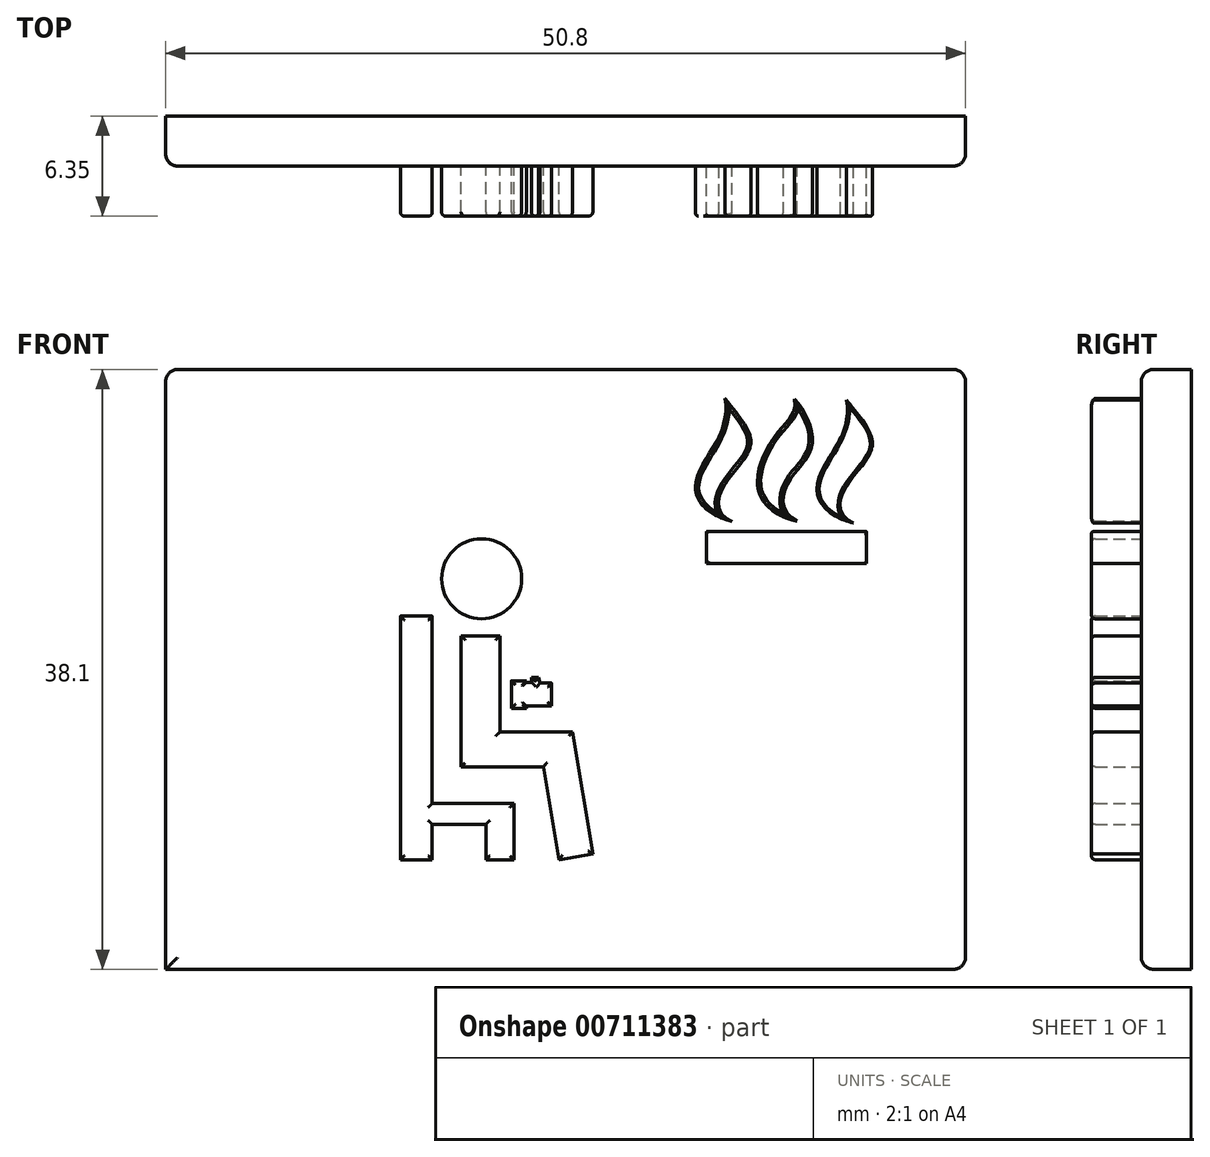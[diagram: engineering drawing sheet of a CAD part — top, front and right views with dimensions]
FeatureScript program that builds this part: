
annotation { "Feature Type Name" : "Feature", "Feature Type Description" : "" }
export const myFeature = defineFeature(function(context is Context, id is Id, definition is map)
    precondition{}
    {
        {
            var Q0;
            Q0=qCreatedBy(makeId("Front.planeOp"),FACE);
            var sketch = newSketch(context, id + "F0", { "sketchPlane" : qUnion([Q0])});
            skLineSegment(sketch, "E0.bottom", {"start": v(-18.77, 4.86) * mm, "end": v(32.03, 4.86) * mm});
            skLineSegment(sketch, "E0.top", {"start": v(-18.77, -33.24) * mm, "end": v(32.03, -33.24) * mm});
            skLineSegment(sketch, "E0.left", {"start": v(-18.77, 4.86) * mm, "end": v(-18.77, -33.24) * mm});
            skLineSegment(sketch, "E0.right", {"start": v(32.03, 4.86) * mm, "end": v(32.03, -33.24) * mm});
            skSolve(sketch);
        }
        {
            var Q0;
            Q0=makeQuery(id+"F0.imprint","IMPRINT",FACE,{"disambiguationData":[TD([[makeQuery(id+"F0.imprint","IMPRINT",EDGE,{"derivedFrom":sQuery(id+"F0.wireOp",EDGE,"E0.bottom")}),-1.0]])]});
            extrude(context, id + "F1", {"entities" : qUnion([Q0]), "depth" : 3.17 * mm, "offsetDistance" : 25.4 * mm});
        }
        {
            var Q0;
            Q0=makeQuery(id+"F1.opExtrude","CAP_FACE",FACE,{"disambiguationData":[OSD([sQuery(id+"F0.wireOp",EDGE,"E0.bottom"),sQuery(id+"F0.wireOp",EDGE,"E0.top"),sQuery(id+"F0.wireOp",EDGE,"E0.left"),sQuery(id+"F0.wireOp",EDGE,"E0.right")])],"isStart":false});
            var sketch = newSketch(context, id + "F2", { "sketchPlane" : qUnion([Q0])});
            skCircle(sketch, "E1", {"center": v(1.3, -8.43) * mm, "radius": 2.54 * mm});
            skLineSegment(sketch, "E2", {"start": v(0, -12.05) * mm, "end": v(0, -20.37) * mm});
            skLineSegment(sketch, "E3", {"start": v(0, -20.37) * mm, "end": v(5.23, -20.37) * mm});
            skLineSegment(sketch, "E4", {"start": v(5.23, -20.37) * mm, "end": v(6.22, -26.27) * mm});
            skLineSegment(sketch, "E5", {"start": v(6.22, -26.27) * mm, "end": v(8.36, -25.92) * mm});
            skLineSegment(sketch, "E6", {"start": v(8.36, -25.92) * mm, "end": v(7.07, -18.16) * mm});
            skLineSegment(sketch, "E7", {"start": v(7.07, -18.16) * mm, "end": v(2.46, -18.16) * mm});
            skLineSegment(sketch, "E8", {"start": v(2.46, -18.16) * mm, "end": v(2.46, -12.05) * mm});
            skLineSegment(sketch, "E9", {"start": v(2.46, -12.05) * mm, "end": v(0, -12.05) * mm});
            skLineSegment(sketch, "E10", {"start": v(-1.83, -12.05) * mm, "end": v(-1.83, -22.7) * mm});
            skLineSegment(sketch, "E11", {"start": v(-1.83, -22.7) * mm, "end": v(3.35, -22.7) * mm});
            skLineSegment(sketch, "E12", {"start": v(3.35, -22.7) * mm, "end": v(3.35, -26.27) * mm});
            skLineSegment(sketch, "E13", {"start": v(3.35, -26.27) * mm, "end": v(1.56, -26.27) * mm});
            skLineSegment(sketch, "E14", {"start": v(1.56, -26.27) * mm, "end": v(1.56, -24.04) * mm});
            skLineSegment(sketch, "E15", {"start": v(1.56, -24.04) * mm, "end": v(-1.83, -24.04) * mm});
            skLineSegment(sketch, "E16", {"start": v(-1.83, -24.04) * mm, "end": v(-1.83, -26.27) * mm});
            skLineSegment(sketch, "E17", {"start": v(-1.83, -26.27) * mm, "end": v(-3.86, -26.27) * mm});
            skLineSegment(sketch, "E18", {"start": v(-3.86, -26.27) * mm, "end": v(-3.86, -10.8) * mm});
            skLineSegment(sketch, "E19", {"start": v(-3.86, -10.8) * mm, "end": v(-1.83, -10.8) * mm});
            skLineSegment(sketch, "E20", {"start": v(-1.83, -10.8) * mm, "end": v(-1.83, -12.05) * mm});
            skLineSegment(sketch, "E21.bottom", {"start": v(3.2, -14.9) * mm, "end": v(4.14, -14.9) * mm});
            skLineSegment(sketch, "E21.top", {"start": v(3.2, -16.65) * mm, "end": v(4.14, -16.65) * mm});
            skLineSegment(sketch, "E21.left", {"start": v(3.2, -14.9) * mm, "end": v(3.2, -16.65) * mm});
            skLineSegment(sketch, "E21.right", {"start": v(4.14, -14.9) * mm, "end": v(4.14, -16.65) * mm});
            skLineSegment(sketch, "E22", {"start": v(4.14, -15) * mm, "end": v(4.46, -15) * mm});
            skLineSegment(sketch, "E23", {"start": v(4.46, -15) * mm, "end": v(4.46, -14.7) * mm});
            skLineSegment(sketch, "E24", {"start": v(4.46, -14.7) * mm, "end": v(4.92, -14.7) * mm});
            skLineSegment(sketch, "E25", {"start": v(4.92, -14.7) * mm, "end": v(5, -15.05) * mm});
            skLineSegment(sketch, "E26", {"start": v(5, -15.05) * mm, "end": v(5.76, -15.05) * mm});
            skLineSegment(sketch, "E27", {"start": v(5.76, -15.05) * mm, "end": v(5.76, -16.52) * mm});
            skLineSegment(sketch, "E28", {"start": v(5.76, -16.52) * mm, "end": v(4.14, -16.52) * mm});
            skSolve(sketch);
        }
        {
            var Q0;
            Q0=makeQuery(id+"F2.imprint","IMPRINT",FACE,{"disambiguationData":[TD([[makeQuery(id+"F2.imprint","IMPRINT",EDGE,{"derivedFrom":sQuery(id+"F2.wireOp",EDGE,"E2")}),1.0]])]});
            var Q1;
            Q1=makeQuery(id+"F2.imprint","IMPRINT",FACE,{"disambiguationData":[TD([[makeQuery(id+"F2.imprint","IMPRINT",EDGE,{"derivedFrom":sQuery(id+"F2.wireOp",EDGE,"E10")}),-1.0]])]});
            var Q2;
            Q2=makeQuery(id+"F2.imprint","IMPRINT",FACE,{"disambiguationData":[TD([[makeQuery(id+"F2.imprint","IMPRINT",EDGE,{"derivedFrom":sQuery(id+"F2.wireOp",EDGE,"E1")}),1.0]])]});
            extrude(context, id + "F3", {"entities" : qUnion([Q0, Q1, Q2]), "operationType" : NewBodyOperationType.ADD, "depth" : 3.17 * mm, "offsetDistance" : 25.4 * mm});
        }
        {
            var Q0;
            Q0 = qSketchRegion(id + "F2", true);
            extrude(context, id + "F4", {"entities" : qUnion([Q0]), "operationType" : NewBodyOperationType.ADD, "depth" : 3.17 * mm, "offsetDistance" : 25.4 * mm});
        }
        {
            var Q0;
            Q0=makeQuery(id+"F3.opExtrude","CAP_EDGE",EDGE,{"disambiguationData":[OSD([sQuery(id+"F2.wireOp",EDGE,"E18")])],"isStart":false});
            var Q1;
            Q1=makeQuery(id+"F3.opExtrude","CAP_EDGE",EDGE,{"disambiguationData":[OSD([sQuery(id+"F2.wireOp",EDGE,"E19")])],"isStart":false});
            var Q2;
            Q2=makeQuery(id+"F3.opExtrude","CAP_EDGE",EDGE,{"disambiguationData":[OSD([sQuery(id+"F2.wireOp",EDGE,"E10"),sQuery(id+"F2.wireOp",EDGE,"E20")])],"isStart":false});
            var Q3;
            Q3=makeQuery(id+"F3.opExtrude","CAP_EDGE",EDGE,{"disambiguationData":[OSD([sQuery(id+"F2.wireOp",EDGE,"E1")])],"isStart":false});
            var Q4;
            Q4=makeQuery(id+"F3.opExtrude","CAP_EDGE",EDGE,{"disambiguationData":[OSD([sQuery(id+"F2.wireOp",EDGE,"E2")])],"isStart":false});
            var Q5;
            Q5=makeQuery(id+"F3.opExtrude","CAP_EDGE",EDGE,{"disambiguationData":[OSD([sQuery(id+"F2.wireOp",EDGE,"E9")])],"isStart":false});
            var Q6;
            Q6=makeQuery(id+"F3.opExtrude","CAP_EDGE",EDGE,{"disambiguationData":[OSD([sQuery(id+"F2.wireOp",EDGE,"E8")])],"isStart":false});
            var Q7;
            Q7=makeQuery(id+"F3.opExtrude","CAP_EDGE",EDGE,{"disambiguationData":[OSD([sQuery(id+"F2.wireOp",EDGE,"E7")])],"isStart":false});
            var Q8;
            Q8=makeQuery(id+"F3.opExtrude","CAP_EDGE",EDGE,{"disambiguationData":[OSD([sQuery(id+"F2.wireOp",EDGE,"E6")])],"isStart":false});
            var Q9;
            Q9=makeQuery(id+"F3.opExtrude","CAP_EDGE",EDGE,{"disambiguationData":[OSD([sQuery(id+"F2.wireOp",EDGE,"E5")])],"isStart":false});
            var Q10;
            Q10=makeQuery(id+"F3.opExtrude","CAP_EDGE",EDGE,{"disambiguationData":[OSD([sQuery(id+"F2.wireOp",EDGE,"E4")])],"isStart":false});
            var Q11;
            Q11=makeQuery(id+"F3.opExtrude","CAP_EDGE",EDGE,{"disambiguationData":[OSD([sQuery(id+"F2.wireOp",EDGE,"E3")])],"isStart":false});
            var Q12;
            Q12=makeQuery(id+"F3.opExtrude","CAP_EDGE",EDGE,{"disambiguationData":[OSD([sQuery(id+"F2.wireOp",EDGE,"E17")])],"isStart":false});
            var Q13;
            Q13=makeQuery(id+"F3.opExtrude","CAP_EDGE",EDGE,{"disambiguationData":[OSD([sQuery(id+"F2.wireOp",EDGE,"E16")])],"isStart":false});
            var Q14;
            Q14=makeQuery(id+"F3.opExtrude","CAP_EDGE",EDGE,{"disambiguationData":[OSD([sQuery(id+"F2.wireOp",EDGE,"E15")])],"isStart":false});
            var Q15;
            Q15=makeQuery(id+"F3.opExtrude","CAP_EDGE",EDGE,{"disambiguationData":[OSD([sQuery(id+"F2.wireOp",EDGE,"E11")])],"isStart":false});
            var Q16;
            Q16=makeQuery(id+"F3.opExtrude","CAP_EDGE",EDGE,{"disambiguationData":[OSD([sQuery(id+"F2.wireOp",EDGE,"E14")])],"isStart":false});
            var Q17;
            Q17=makeQuery(id+"F3.opExtrude","CAP_EDGE",EDGE,{"disambiguationData":[OSD([sQuery(id+"F2.wireOp",EDGE,"E13")])],"isStart":false});
            var Q18;
            Q18=makeQuery(id+"F3.opExtrude","CAP_EDGE",EDGE,{"disambiguationData":[OSD([sQuery(id+"F2.wireOp",EDGE,"E12")])],"isStart":false});
            var Q19;
            Q19=makeQuery(id+"F4.opExtrude","CAP_EDGE",EDGE,{"disambiguationData":[OSD([sQuery(id+"F2.wireOp",EDGE,"E28")])],"isStart":false});
            var Q20;
            Q20=makeQuery(id+"F4.opExtrude","CAP_EDGE",EDGE,{"disambiguationData":[OSD([sQuery(id+"F2.wireOp",EDGE,"E21.top")])],"isStart":false});
            var Q21;
            {var subQ0=sQuery(id+"F2.wireOp",EDGE,"E21.right");Q21=makeQuery(id+"F4.opExtrude","CAP_EDGE",EDGE,{"disambiguationData":[OSD([subQ0]),TDD([makeQuery(id+"F2.imprint","IMPRINT",EDGE,{"disambiguationData":[TD([[makeQuery(id+"F2.imprint","INTERSECT",VERTEX,{"derivedFrom":[sQuery(id+"F2.wireOp",EDGE,"E21.top"),subQ0]}),1.0]])],"derivedFrom":subQ0})])],"isStart":false});}
            var Q22;
            Q22=makeQuery(id+"F4.opExtrude","CAP_EDGE",EDGE,{"disambiguationData":[OSD([sQuery(id+"F2.wireOp",EDGE,"E27")])],"isStart":false});
            var Q23;
            Q23=makeQuery(id+"F4.opExtrude","CAP_EDGE",EDGE,{"disambiguationData":[OSD([sQuery(id+"F2.wireOp",EDGE,"E26")])],"isStart":false});
            var Q24;
            Q24=makeQuery(id+"F4.opExtrude","CAP_EDGE",EDGE,{"disambiguationData":[OSD([sQuery(id+"F2.wireOp",EDGE,"E25")])],"isStart":false});
            var Q25;
            Q25=makeQuery(id+"F4.opExtrude","CAP_EDGE",EDGE,{"disambiguationData":[OSD([sQuery(id+"F2.wireOp",EDGE,"E24")])],"isStart":false});
            var Q26;
            Q26=makeQuery(id+"F4.opExtrude","CAP_EDGE",EDGE,{"disambiguationData":[OSD([sQuery(id+"F2.wireOp",EDGE,"E23")])],"isStart":false});
            var Q27;
            Q27=makeQuery(id+"F4.opExtrude","CAP_EDGE",EDGE,{"disambiguationData":[OSD([sQuery(id+"F2.wireOp",EDGE,"E22")])],"isStart":false});
            var Q28;
            {var subQ0=sQuery(id+"F2.wireOp",EDGE,"E21.right");Q28=makeQuery(id+"F4.opExtrude","CAP_EDGE",EDGE,{"disambiguationData":[OSD([subQ0]),TDD([makeQuery(id+"F2.imprint","IMPRINT",EDGE,{"disambiguationData":[TD([[makeQuery(id+"F2.imprint","INTERSECT",VERTEX,{"derivedFrom":[sQuery(id+"F2.wireOp",EDGE,"E21.bottom"),subQ0]}),-1.0]])],"derivedFrom":subQ0})])],"isStart":false});}
            var Q29;
            Q29=makeQuery(id+"F4.opExtrude","CAP_EDGE",EDGE,{"disambiguationData":[OSD([sQuery(id+"F2.wireOp",EDGE,"E21.bottom")])],"isStart":false});
            var Q30;
            Q30=makeQuery(id+"F4.opExtrude","CAP_EDGE",EDGE,{"disambiguationData":[OSD([sQuery(id+"F2.wireOp",EDGE,"E21.left")])],"isStart":false});
            fillet(context, id + "F5", {"entities" : qUnion([Q0, Q1, Q2, Q3, Q4, Q5, Q6, Q7, Q8, Q9, Q10, Q11, Q12, Q13, Q14, Q15, Q16, Q17, Q18, Q19, Q20, Q21, Q22, Q23, Q24, Q25, Q26, Q27, Q28, Q29, Q30]), "radius" : 0.25 * mm, "tangentPropagation" : true, "allowEdgeOverflow" : false});
        }
        {
            var Q0;
            Q0=makeQuery(id+"F1.opExtrude","CAP_FACE",FACE,{"disambiguationData":[OSD([sQuery(id+"F0.wireOp",EDGE,"E0.bottom"),sQuery(id+"F0.wireOp",EDGE,"E0.top"),sQuery(id+"F0.wireOp",EDGE,"E0.left"),sQuery(id+"F0.wireOp",EDGE,"E0.right")])],"isStart":false});
            var sketch = newSketch(context, id + "F6", { "sketchPlane" : qUnion([Q0])});
            skLineSegment(sketch, "E29.bottom", {"start": v(15.6, -5.44) * mm, "end": v(25.76, -5.44) * mm});
            skLineSegment(sketch, "E29.top", {"start": v(15.6, -7.47) * mm, "end": v(25.76, -7.47) * mm});
            skLineSegment(sketch, "E29.left", {"start": v(15.6, -5.44) * mm, "end": v(15.6, -7.47) * mm});
            skLineSegment(sketch, "E29.right", {"start": v(25.76, -5.44) * mm, "end": v(25.76, -7.47) * mm});
            skFitSpline(sketch, "E30", {"points": [v(24.92, -4.88) * mm, v(24.38, -2.7) * mm, v(26.12, 0) * mm, v(24.48, 2.93) * mm], "startDerivative": vector(-11.05, 4.33) * mm, "endDerivative": vector(-7.07, 9.32) * mm});
            skFitSpline(sketch, "E31", {"points": [v(24.92, -4.88) * mm, v(22.6, -2.7) * mm, v(23.84, 0) * mm, v(24.48, 2.93) * mm], "startDerivative": vector(-13.95, 3.45) * mm, "endDerivative": vector(-1.83, 9.89) * mm});
            skFitSpline(sketch, "E32", {"points": [v(21.31, -4.77) * mm, v(20.74, -2.36) * mm, v(22.21, -0.22) * mm, v(21.16, 2.98) * mm], "startDerivative": vector(-10.5, 5.58) * mm, "endDerivative": vector(-7.87, 8.62) * mm});
            skFitSpline(sketch, "E33", {"points": [v(21.31, -4.77) * mm, v(18.82, -2.36) * mm, v(20.22, 0.98) * mm, v(21.16, 2.98) * mm], "startDerivative": vector(-13.95, 3.45) * mm, "endDerivative": vector(-1.83, 9.89) * mm});
            skFitSpline(sketch, "E34", {"points": [v(17.2, -4.77) * mm, v(16.66, -2.58) * mm, v(18.4, 0.1) * mm, v(16.76, 3.03) * mm], "startDerivative": vector(-11.05, 4.33) * mm, "endDerivative": vector(-7.07, 9.32) * mm});
            skFitSpline(sketch, "E35", {"points": [v(17.2, -4.77) * mm, v(14.88, -2.58) * mm, v(16.12, 0.1) * mm, v(16.76, 3.03) * mm], "startDerivative": vector(-13.95, 3.45) * mm, "endDerivative": vector(-1.83, 9.89) * mm});
            skSolve(sketch);
        }
        {
            var Q0;
            Q0 = qSketchRegion(id + "F6", true);
            extrude(context, id + "F7", {"entities" : qUnion([Q0]), "operationType" : NewBodyOperationType.ADD, "depth" : 3.17 * mm, "offsetDistance" : 25.4 * mm});
        }
        {
            var Q0;
            Q0=makeQuery(id+"F7.opExtrude","CAP_EDGE",EDGE,{"disambiguationData":[OSD([sQuery(id+"F6.wireOp",EDGE,"767095f4-a686-475d-b9b1-60b74ad925fc")])],"isStart":false});
            var Q1;
            Q1=makeQuery(id+"F7.opExtrude","CAP_EDGE",EDGE,{"disambiguationData":[OSD([sQuery(id+"F6.wireOp",EDGE,"99f99596-8cdb-4deb-93aa-1a6c93595f37")])],"isStart":false});
            var Q2;
            Q2=makeQuery(id+"F7.opExtrude","CAP_EDGE",EDGE,{"disambiguationData":[OSD([sQuery(id+"F6.wireOp",EDGE,"c4b43bae-7532-41a1-bbe2-5a4035174fb6")])],"isStart":false});
            var Q3;
            Q3=makeQuery(id+"F7.opExtrude","CAP_EDGE",EDGE,{"disambiguationData":[OSD([sQuery(id+"F6.wireOp",EDGE,"E31")])],"isStart":false});
            var Q4;
            Q4=makeQuery(id+"F7.opExtrude","CAP_EDGE",EDGE,{"disambiguationData":[OSD([sQuery(id+"F6.wireOp",EDGE,"E30")])],"isStart":false});
            var Q5;
            Q5=makeQuery(id+"F7.opExtrude","CAP_EDGE",EDGE,{"disambiguationData":[OSD([sQuery(id+"F6.wireOp",EDGE,"E29.right")])],"isStart":false});
            var Q6;
            Q6=makeQuery(id+"F7.opExtrude","CAP_EDGE",EDGE,{"disambiguationData":[OSD([sQuery(id+"F6.wireOp",EDGE,"E29.bottom")])],"isStart":false});
            var Q7;
            Q7=makeQuery(id+"F7.opExtrude","CAP_EDGE",EDGE,{"disambiguationData":[OSD([sQuery(id+"F6.wireOp",EDGE,"E29.top")])],"isStart":false});
            var Q8;
            Q8=makeQuery(id+"F7.opExtrude","CAP_EDGE",EDGE,{"disambiguationData":[OSD([sQuery(id+"F6.wireOp",EDGE,"E29.left")])],"isStart":false});
            var Q9;
            Q9=makeQuery(id+"F7.opExtrude","CAP_EDGE",EDGE,{"disambiguationData":[OSD([sQuery(id+"F6.wireOp",EDGE,"de12b81a-7bfb-4d2a-b35c-4e75c18c1337")])],"isStart":false});
            fillet(context, id + "F8", {"entities" : qUnion([Q0, Q1, Q2, Q3, Q4, Q5, Q6, Q7, Q8, Q9]), "radius" : 0.13 * mm, "tangentPropagation" : true, "allowEdgeOverflow" : false});
        }
        {
            var Q0;
            Q0=makeQuery(id+"F7.opExtrude","CAP_EDGE",EDGE,{"disambiguationData":[OSD([sQuery(id+"F6.wireOp",EDGE,"E32")])],"isStart":false});
            var Q1;
            Q1=makeQuery(id+"F7.opExtrude","CAP_EDGE",EDGE,{"disambiguationData":[OSD([sQuery(id+"F6.wireOp",EDGE,"E33")])],"isStart":false});
            var Q2;
            Q2=makeQuery(id+"F7.opExtrude","CAP_EDGE",EDGE,{"disambiguationData":[OSD([sQuery(id+"F6.wireOp",EDGE,"E34")])],"isStart":false});
            var Q3;
            Q3=makeQuery(id+"F7.opExtrude","CAP_EDGE",EDGE,{"disambiguationData":[OSD([sQuery(id+"F6.wireOp",EDGE,"E35")])],"isStart":false});
            var Q4;
            {var subQ0=sQuery(id+"F6.wireOp",EDGE,"E31");Q4=makeQuery(id+"F8.opFillet","BLEND_EDGE",EDGE,{"blendedFrom":[makeQuery(id+"F7.opExtrude","CAP_EDGE",EDGE,{"disambiguationData":[OSD([subQ0])],"isStart":false}),makeQuery(id+"F7.opExtrude","CAP_FACE",FACE,{"disambiguationData":[OSD([sQuery(id+"F6.wireOp",EDGE,"E30"),subQ0])],"isStart":false})],"blendedInto":[makeQuery(id+"F7.opExtrude","CAP_FACE",FACE,{"disambiguationData":[OSD([sQuery(id+"F6.wireOp",EDGE,"E30"),subQ0])],"isStart":false})]});}
            var Q5;
            {var subQ0=sQuery(id+"F6.wireOp",EDGE,"E30");Q5=makeQuery(id+"F8.opFillet","BLEND_EDGE",EDGE,{"blendedFrom":[makeQuery(id+"F7.opExtrude","CAP_EDGE",EDGE,{"disambiguationData":[OSD([subQ0])],"isStart":false}),makeQuery(id+"F7.opExtrude","SWEPT_FACE",FACE,{"disambiguationData":[OSD([subQ0])]})],"blendedInto":[makeQuery(id+"F7.opExtrude","SWEPT_FACE",FACE,{"disambiguationData":[OSD([subQ0])]})]});}
            fillet(context, id + "F9", {"entities" : qUnion([Q0, Q1, Q2, Q3, Q4, Q5]), "radius" : 0.2 * mm, "tangentPropagation" : true, "allowEdgeOverflow" : false});
        }
        {
            var Q0;
            Q0=makeQuery(id+"F1.opExtrude","CAP_EDGE",EDGE,{"disambiguationData":[OSD([sQuery(id+"F0.wireOp",EDGE,"E0.right")])],"isStart":false});
            var Q1;
            Q1=makeQuery(id+"F1.opExtrude","CAP_EDGE",EDGE,{"disambiguationData":[OSD([sQuery(id+"F0.wireOp",EDGE,"E0.top")])],"isStart":false});
            var Q2;
            Q2=makeQuery(id+"F1.opExtrude","CAP_EDGE",EDGE,{"disambiguationData":[OSD([sQuery(id+"F0.wireOp",EDGE,"E0.bottom")])],"isStart":false});
            var Q3;
            Q3=makeQuery(id+"F1.opExtrude","CAP_EDGE",EDGE,{"disambiguationData":[OSD([sQuery(id+"F0.wireOp",EDGE,"E0.left")])],"isStart":false});
            fillet(context, id + "F10", {"entities" : qUnion([Q0, Q1, Q2, Q3]), "radius" : 0.76 * mm, "tangentPropagation" : true, "allowEdgeOverflow" : false});
        }
        {
            var Q0;
            Q0=makeQuery(id+"F1.opExtrude","SWEPT_EDGE",EDGE,{"disambiguationData":[OSD([sQuery(id+"F0.wireOp",EDGE,"E0.bottom"),sQuery(id+"F0.wireOp",EDGE,"E0.right")])]});
            var Q1;
            Q1=makeQuery(id+"F1.opExtrude","SWEPT_EDGE",EDGE,{"disambiguationData":[OSD([sQuery(id+"F0.wireOp",EDGE,"E0.bottom"),sQuery(id+"F0.wireOp",EDGE,"E0.left")])]});
            var Q2;
            Q2=makeQuery(id+"F1.opExtrude","SWEPT_EDGE",EDGE,{"disambiguationData":[OSD([sQuery(id+"F0.wireOp",EDGE,"E0.top"),sQuery(id+"F0.wireOp",EDGE,"E0.right")])]});
            fillet(context, id + "F11", {"entities" : qUnion([Q0, Q1, Q2]), "radius" : 0.76 * mm, "tangentPropagation" : true, "allowEdgeOverflow" : false});
        }
    });
